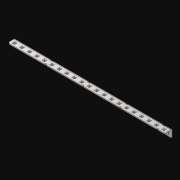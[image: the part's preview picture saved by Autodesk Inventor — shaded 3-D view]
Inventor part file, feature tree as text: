
AUTODESK INVENTOR PART (.ipt)
format: ipt  version: 2021 (Build 250183000, 183)  size: 740,352 bytes
history: native  units: in
note: dims shown in document units (in); Inventor stores cm internally (conversion verified against a paired STEP export)
features: extrude x43, other x42, sketch x3, pattern_linear x1, sheet_metal_op x1
ambient origin geometry x8: Origin, YZ Plane, XZ Plane, XY Plane, X Axis, Y Axis, Z Axis, Center Point
bodies: Solid1 (feature_tree)
feature tree (90):
  pattern_linear  "Rectangular Pattern1"  Spacing1=0.063in  [1 undecoded]
  extrude  "Extrusion1"  Depth=0.5in
  sketch  "Sketch1"  dims[d0=0.182in]
  other  "Srf1"
  sketch  "Sketch2"  dims[d1=0.063in d2=0.0in]
  other  "Srf2"
  other  "Srf3"
  other  "Srf5"
  other  "Srf7"
  other  "Srf9"
  other  "Srf11"
  other  "Srf13"
  other  "Srf15"
  other  "Srf17"
  other  "Srf19"
  other  "Srf21"
  other  "Srf23"
  other  "Srf25"
  other  "Srf27"
  other  "Srf29"
  other  "Srf31"
  other  "Srf33"
  other  "Srf35"
  other  "Srf37"
  other  "Srf39"
  other  "Srf41"
  other  "Srf4"
  other  "Srf6"
  other  "Srf8"
  other  "Srf10"
  other  "Srf12"
  other  "Srf14"
  other  "Srf16"
  other  "Srf18"
  other  "Srf20"
  other  "Srf22"
  other  "Srf24"
  other  "Srf26"
  other  "Srf28"
  other  "Srf30"
  other  "Srf32"
  other  "Srf34"
  other  "Srf36"
  other  "Srf38"
  other  "Srf40"
  other  "Srf42"
  sketch  "Sketch3"  dims[d3=0.182in d4=0.063in d5=0.0in d8=0.5in d9=7.0in d10=0.0in]
  sheet_metal_op  "Fold1"
  extrude  "ExtrusionSrf1"  Depth=7.0in TaperAngle=0.0deg
  extrude  "ExtrusionSrf2"  [1 undecoded]
  extrude  "ExtrusionSrf3"  [1 undecoded]
  extrude  "ExtrusionSrf4"  [1 undecoded]
  extrude  "ExtrusionSrf5"  [1 undecoded]
  extrude  "ExtrusionSrf6"  [1 undecoded]
  extrude  "ExtrusionSrf7"  [1 undecoded]
  extrude  "ExtrusionSrf8"  [1 undecoded]
  extrude  "ExtrusionSrf9"  [1 undecoded]
  extrude  "ExtrusionSrf10"  [1 undecoded]
  extrude  "ExtrusionSrf11"  [1 undecoded]
  extrude  "ExtrusionSrf12"  [1 undecoded]
  extrude  "ExtrusionSrf13"  [1 undecoded]
  extrude  "ExtrusionSrf14"  [1 undecoded]
  extrude  "ExtrusionSrf15"  [1 undecoded]
  extrude  "ExtrusionSrf16"  [1 undecoded]
  extrude  "ExtrusionSrf17"  [1 undecoded]
  extrude  "ExtrusionSrf18"  [1 undecoded]
  extrude  "ExtrusionSrf19"  [1 undecoded]
  extrude  "ExtrusionSrf20"  [1 undecoded]
  extrude  "ExtrusionSrf21"  [1 undecoded]
  extrude  "ExtrusionSrf22"  [1 undecoded]
  extrude  "ExtrusionSrf37"  [1 undecoded]
  extrude  "ExtrusionSrf38"  [1 undecoded]
  extrude  "ExtrusionSrf39"  [1 undecoded]
  extrude  "ExtrusionSrf40"  [1 undecoded]
  extrude  "ExtrusionSrf41"  [1 undecoded]
  extrude  "ExtrusionSrf42"  [1 undecoded]
  extrude  "ExtrusionSrf43"  [1 undecoded]
  extrude  "ExtrusionSrf44"  [1 undecoded]
  extrude  "ExtrusionSrf45"  [1 undecoded]
  extrude  "ExtrusionSrf46"  [1 undecoded]
  extrude  "ExtrusionSrf47"  [1 undecoded]
  extrude  "ExtrusionSrf48"  [1 undecoded]
  extrude  "ExtrusionSrf49"  [1 undecoded]
  extrude  "ExtrusionSrf50"  [1 undecoded]
  extrude  "ExtrusionSrf51"  [1 undecoded]
  extrude  "ExtrusionSrf52"  [1 undecoded]
  extrude  "ExtrusionSrf53"  [1 undecoded]
  extrude  "ExtrusionSrf54"  [1 undecoded]
  extrude  "ExtrusionSrf55"  [1 undecoded]
  extrude  "ExtrusionSrf56"  [1 undecoded]
note: 42 required parameter values undecoded (feature->parameter linkage not recoverable at this tier; creation-order binding heuristic only, values carry confidence <= 0.55)
